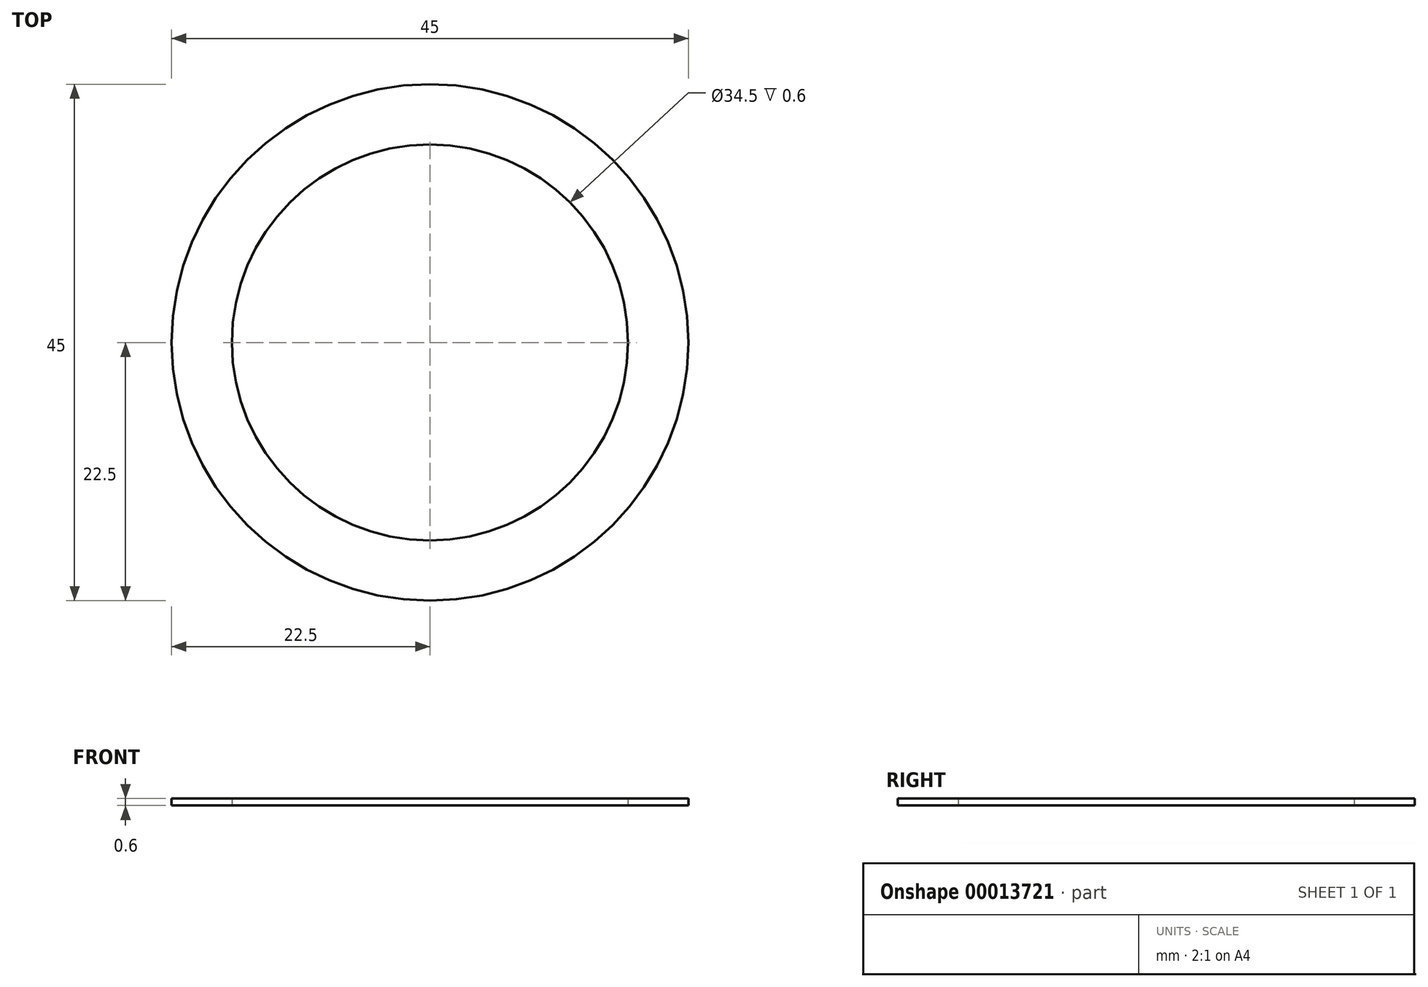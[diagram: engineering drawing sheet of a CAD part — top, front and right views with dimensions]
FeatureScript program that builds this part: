
annotation { "Feature Type Name" : "Feature", "Feature Type Description" : "" }
export const myFeature = defineFeature(function(context is Context, id is Id, definition is map)
    precondition{}
    {
        {
            var Q0;
            Q0=qCreatedBy(makeId("Top.planeOp"),FACE);
            var sketch = newSketch(context, id + "F0", { "sketchPlane" : qUnion([Q0])});
            skCircle(sketch, "E0", {"center": v(0, 0) * mm, "radius": 17.25 * mm});
            skCircle(sketch, "E1", {"center": v(0, 0) * mm, "radius": 22.5 * mm});
            skSolve(sketch);
        }
        {
            var Q0;
            Q0=makeQuery(id+"F0.imprint","IMPRINT",FACE,{"disambiguationData":[TD([[makeQuery(id+"F0.imprint","IMPRINT",EDGE,{"derivedFrom":sQuery(id+"F0.wireOp",EDGE,"E0")}),-1.0]])]});
            extrude(context, id + "F1", {"entities" : qUnion([Q0]), "depth" : 0.6 * mm});
        }
    });
